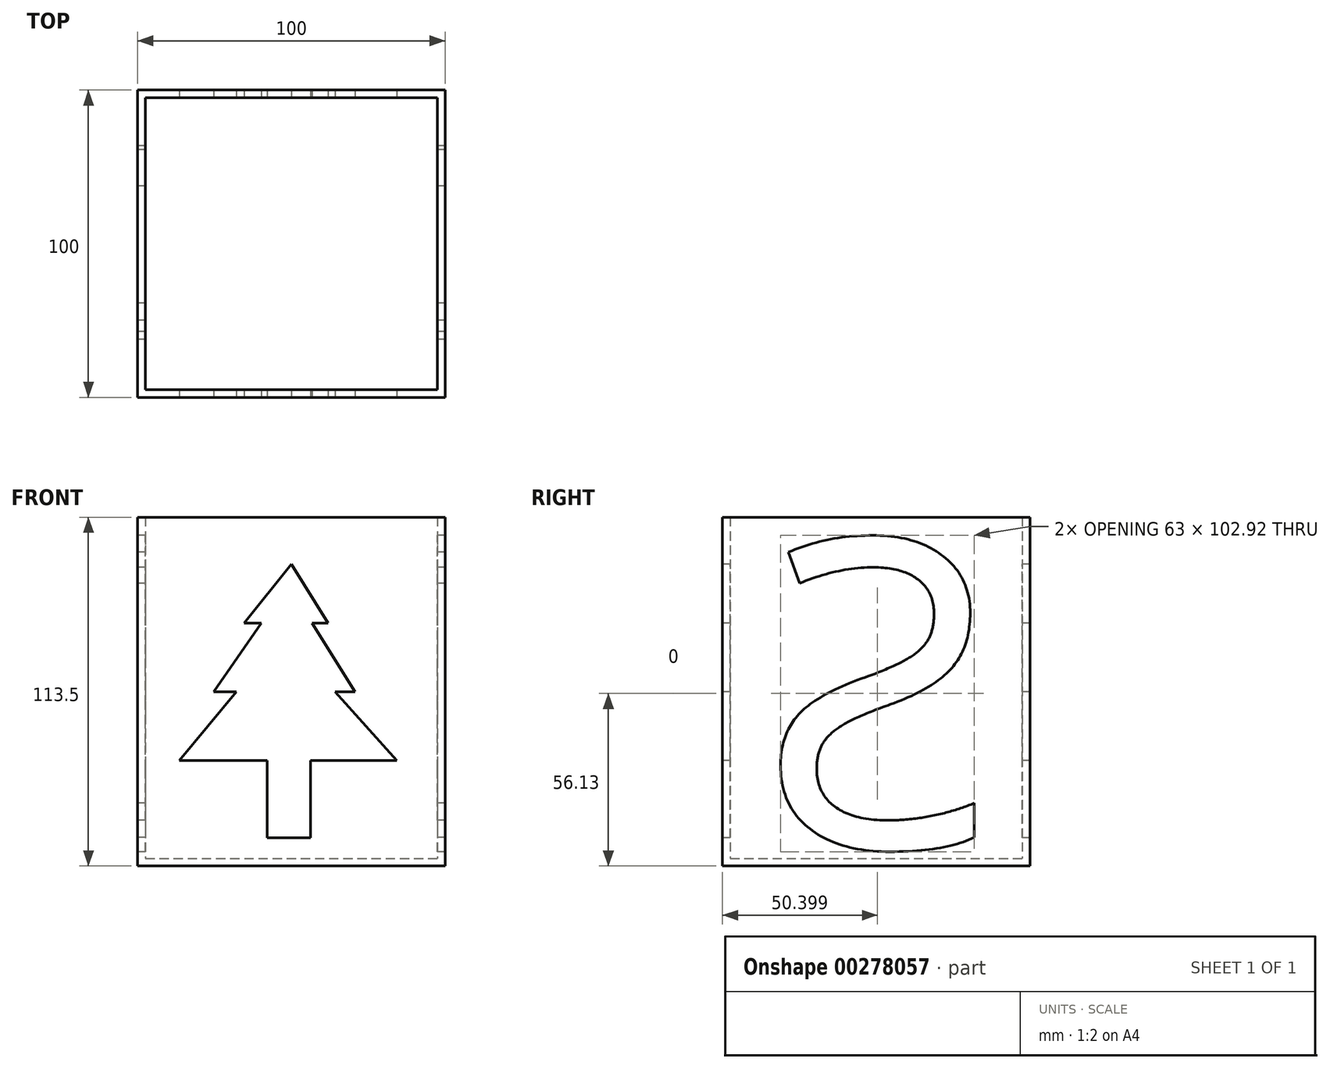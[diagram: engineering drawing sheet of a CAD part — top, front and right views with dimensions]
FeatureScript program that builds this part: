
annotation { "Feature Type Name" : "Feature", "Feature Type Description" : "" }
export const myFeature = defineFeature(function(context is Context, id is Id, definition is map)
    precondition{}
    {
        {
            var Q0;
            Q0=qCreatedBy(makeId("Front.planeOp"),FACE);
            var sketch = newSketch(context, id + "F0", { "sketchPlane" : qUnion([Q0])});
            skLineSegment(sketch, "E0.bottom", {"start": v(-50, 56.75) * mm, "end": v(50, 56.75) * mm});
            skLineSegment(sketch, "E0.top", {"start": v(-50, -56.75) * mm, "end": v(50, -56.75) * mm});
            skLineSegment(sketch, "E0.left", {"start": v(-50, 56.75) * mm, "end": v(-50, -56.75) * mm});
            skLineSegment(sketch, "E0.right", {"start": v(50, 56.75) * mm, "end": v(50, -56.75) * mm});
            skPoint(sketch, "E0.middle", {"position": v(0, 0) * mm});
            skSolve(sketch);
        }
        {
            var Q0;
            Q0=makeQuery(id+"F0.imprint","IMPRINT",FACE,{"disambiguationData":[TD([[makeQuery(id+"F0.imprint","IMPRINT",EDGE,{"derivedFrom":sQuery(id+"F0.wireOp",EDGE,"E0.bottom")}),-1.0]])]});
            extrude(context, id + "F1", {"entities" : qUnion([Q0]), "endBound" : BoundingType.SYMMETRIC, "depth" : 100 * mm});
        }
        {
            var Q0;
            Q0=makeQuery(id+"F1.opExtrude","SWEPT_FACE",FACE,{"disambiguationData":[OSD([sQuery(id+"F0.wireOp",EDGE,"E0.bottom")])]});
            shell(context, id + "F2", {"entities" : qUnion([Q0]), "thickness" : 2.5 * mm});
        }
        {
            var Q0;
            Q0=makeQuery(id+"F1.opExtrude","CAP_FACE",FACE,{"disambiguationData":[OSD([sQuery(id+"F0.wireOp",EDGE,"E0.bottom"),sQuery(id+"F0.wireOp",EDGE,"E0.top"),sQuery(id+"F0.wireOp",EDGE,"E0.left"),sQuery(id+"F0.wireOp",EDGE,"E0.right")])],"isStart":false});
            var sketch = newSketch(context, id + "F3", { "sketchPlane" : qUnion([Q0])});
            skLineSegment(sketch, "E1.bottom", {"start": v(6.2, -47.58) * mm, "end": v(-7.82, -47.58) * mm});
            skLineSegment(sketch, "E1.top", {"start": v(6.2, -22.44) * mm, "end": v(-7.82, -22.44) * mm});
            skLineSegment(sketch, "E1.left", {"start": v(6.2, -47.58) * mm, "end": v(6.2, -22.44) * mm});
            skLineSegment(sketch, "E1.right", {"start": v(-7.82, -47.58) * mm, "end": v(-7.82, -22.44) * mm});
            skLineSegment(sketch, "E2", {"start": v(-36.48, -22.44) * mm, "end": v(34.33, -22.44) * mm});
            skLineSegment(sketch, "E3", {"start": v(-25.3, 0) * mm, "end": v(20.75, 0) * mm});
            skLineSegment(sketch, "E4", {"start": v(-15.41, 22.27) * mm, "end": v(11.96, 22.27) * mm});
            skLineSegment(sketch, "E5", {"start": v(-36.48, -22.44) * mm, "end": v(-17.9, 0) * mm});
            skLineSegment(sketch, "E6", {"start": v(34.33, -22.44) * mm, "end": v(14.24, 0) * mm});
            skLineSegment(sketch, "E7", {"start": v(-25.3, 0) * mm, "end": v(-9.75, 22.27) * mm});
            skLineSegment(sketch, "E8", {"start": v(20.75, 0) * mm, "end": v(6.75, 22.27) * mm});
            skLineSegment(sketch, "E9", {"start": v(-15.41, 22.27) * mm, "end": v(0, 41.46) * mm});
            skLineSegment(sketch, "E10", {"start": v(11.96, 22.27) * mm, "end": v(0, 41.46) * mm});
            skSolve(sketch);
        }
        {
            var Q0;
            {var subQ3=sQuery(id+"F3.wireOp",EDGE,"E9");Q0=makeQuery(id+"F3.imprint","IMPRINT",FACE,{"disambiguationData":[TD([[makeQuery(id+"F3.imprint","IMPRINT",EDGE,{"derivedFrom":subQ3}),-1.0]])]});}
            var Q1;
            {var subQ0=sQuery(id+"F3.wireOp",EDGE,"E7");Q1=makeQuery(id+"F3.imprint","IMPRINT",FACE,{"disambiguationData":[TD([[makeQuery(id+"F3.imprint","IMPRINT",EDGE,{"derivedFrom":subQ0}),-1.0]])]});}
            var Q2;
            {var subQ4=sQuery(id+"F3.wireOp",EDGE,"E5");Q2=makeQuery(id+"F3.imprint","IMPRINT",FACE,{"disambiguationData":[TD([[makeQuery(id+"F3.imprint","IMPRINT",EDGE,{"derivedFrom":subQ4}),-1.0]])]});}
            var Q3;
            Q3=makeQuery(id+"F3.imprint","IMPRINT",FACE,{"disambiguationData":[TD([[makeQuery(id+"F3.imprint","IMPRINT",EDGE,{"derivedFrom":sQuery(id+"F3.wireOp",EDGE,"E1.bottom")}),-1.0]])]});
            extrude(context, id + "F4", {"entities" : qUnion([Q0, Q1, Q2, Q3]), "operationType" : NewBodyOperationType.REMOVE, "endBound" : BoundingType.THROUGH_ALL, "oppositeDirection" : true, "depth" : 5 * mm});
        }
        {
            var Q0;
            Q0=makeQuery(id+"F1.opExtrude","SWEPT_FACE",FACE,{"disambiguationData":[OSD([sQuery(id+"F0.wireOp",EDGE,"E0.left")])]});
            var sketch = newSketch(context, id + "F5", { "sketchPlane" : qUnion([Q0])});
            skText(sketch, "E11", { "text": "S", "fontName": "OpenSans-Regular.ttf"});
            const initialGuessF5  = {"E11": [-0.03915, -0.0507, 1, 0, 0.10097]};
            skSetInitialGuess(sketch, initialGuessF5);
            skSolve(sketch);
        }
        {
            var Q0;
            Q0=makeQuery(id+"F5.imprint","IMPRINT",FACE,{"disambiguationData":[TD([[makeQuery(id+"F5.imprint","IMPRINT",EDGE,{"derivedFrom":sQuery(id+"F5.wireOp",EDGE,"E11.sketch_text.stroke-0")}),-1.0]])]});
            extrude(context, id + "F6", {"entities" : qUnion([Q0]), "operationType" : NewBodyOperationType.REMOVE, "endBound" : BoundingType.THROUGH_ALL, "oppositeDirection" : true, "depth" : 25 * mm});
        }
    });
